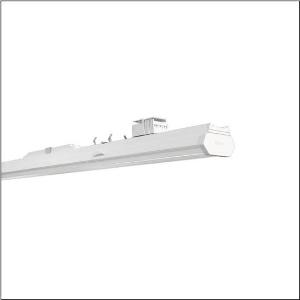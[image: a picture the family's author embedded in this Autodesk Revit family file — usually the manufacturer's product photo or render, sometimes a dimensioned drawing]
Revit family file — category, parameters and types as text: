
# Revit family: licross_11_protected_ho_51td1bdn4e5m3s
name_source: partatom
category: Lighting Fixtures
units: mm (PartAtom-declared; Revit-internal decimal feet)

## family parameters
Cut with Voids When Loaded = No
Host = Face
Light Source = No
Part Type = Normal
Room Calculation Point = No
Round Connector Dimension = Use Diameter
Shared = No

## types (1)
- --- (1 x LED, 920 lm, 7.4 W, 4000K)
    Apparent Load = 7 VA
    CIE Flux Codes = 54 82 95 97 100
    Color Rendering = 80
    Color Temperature = 4000K
    Default Elevation = 1800 mm
    Description = Licross 11 Protected HO, luminaire insert, of sheet steel, galvanised, coil coated, white, length: 1.500mm, width: 90mm, height: 101mm, LED rated luminous flux: 14.500lm, light colour: 840, SDCM (Standard Deviation of Colour Matching)MacAdam ≤ 2 SDCM (initial), control gear: DALI 2 (for two DALI lines), with plug, 6-pole, with phase selection, for trunking rail, 14-core, mains connection: 220..240V, AC, 50/60Hz, rated input power: 91W, for trunking rail, 14-core, internal wiring halogen-free, for emergency light function, converter,control gear: single battery element, battery: LiFePO4, 9Ah, primary optical cover: cover, of PMMA, light emission: direct distribution, primary light characteristic: symmetric, protection rating (complete): IP54, insulation class (complete): insulation class I (protective earthing), certification: CE, UKCA, protection symbol: D if used in an environment with non-conductive dust loads with corresponding accessories, impact resistance: IK06, permissible ambient temperature for indoor applications: +5..+30°C, standard: EN 60598-2-22, LABS conformity tested according to VDMA 24364:2018-05, reducing of maximum allowable ambient temperature of 5°C with ceiling mounting, corresponds to IFS (International Featured Standards) requirements for safety and quality in the food industry, The light source and the operating device comply with the requirements of the Ecodesign Regulation (EU) 2019/2020 and are replaceable in accordance with this regulation, packaging unit: 1 piece
    Height = 92 mm
    Lamp = 1 x LED
    Lamp Light Flux = 920 lm
    Lamp Power = 7.4 W
    Lamp count = 1
    Length = 1500 mm
    Luminous efficacy = 124 lm/W
    Manufacturer = Siteco
    ModVariant = No
    Model = 51TD1BDN4E5M3S
    Mounting Place = Ceiling
    Mounting Type = Pendant
    Number of Poles = 1
    OnlyDefault = Yes
    Power Factor = 1
    Product Name = Licross 11 Protected HO
    Product group = luminaire insert | ceiling pendant
    ProductGroupID = 901
    Protection Class = Protection class I
    Protection Degree = IP 54
    RLX_Detail_Level = 1
    RLX_Emergency_Light_Flux = 0 lm
    RLX_Emergency_Type = 0
    RLX_Emergency_Type_DB = No
    RlxData = <blob elided: 25085 chars, md5=58bcac3e>
    Socket = socket
    Standby Power = 0 W
    System Light Flux = 920 lm
    System Power = 7 W
    Type Comments = : emergency light operation: 3 h
    Type Image = l_1256145.jpg
    URL = http://relux.com
    VarID = @adj_096739
    Voltage = 0 V
    Weight = 0.00 kg
    Width = 88 mm

## geometry (parser evidence)
native form markers: Blend x4, Sweep x11
no freeform markers — native parametric forms only
